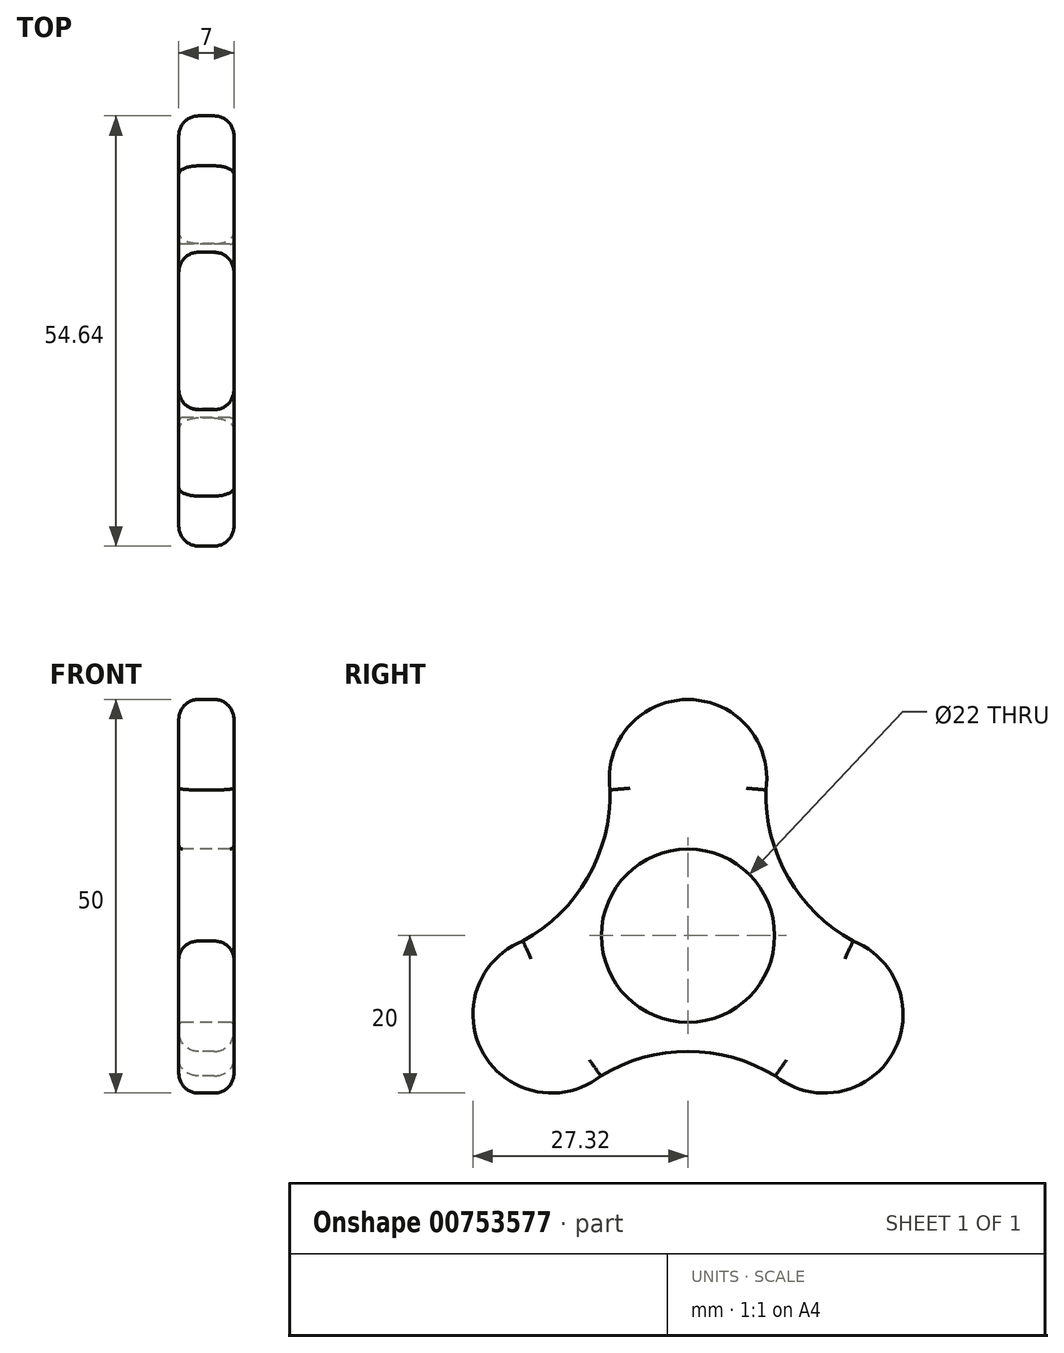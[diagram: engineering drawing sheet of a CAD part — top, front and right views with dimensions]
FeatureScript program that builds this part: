
annotation { "Feature Type Name" : "Feature", "Feature Type Description" : "" }
export const myFeature = defineFeature(function(context is Context, id is Id, definition is map)
    precondition{}
    {
        {
            var Q0;
            Q0=qCreatedBy(makeId("Right.planeOp"),FACE);
            var sketch = newSketch(context, id + "F0", { "sketchPlane" : qUnion([Q0])});
            skLineSegment(sketch, "E0", {"start": v(0, 0) * mm, "end": v(0, 20) * mm, "construction": true});
            skCircle(sketch, "E1", {"center": v(0, 20) * mm, "radius": 10 * mm});
            skCircle(sketch, "E2.1.0", {"center": v(-17.32, -10) * mm, "radius": 10 * mm});
            skCircle(sketch, "E2.2.0", {"center": v(17.32, -10) * mm, "radius": 10 * mm});
            skPoint(sketch, "E2.center", {"position": v(0, 0) * mm});
            skLineSegment(sketch, "E3", {"start": v(0, 20) * mm, "end": v(-17.32, -10) * mm, "construction": true});
            skLineSegment(sketch, "E4", {"start": v(0, 20) * mm, "end": v(-8.66, 25) * mm, "construction": true});
            skLineSegment(sketch, "E5", {"start": v(-17.32, -10) * mm, "end": v(-25.98, -5) * mm, "construction": true});
            skLineSegment(sketch, "E6", {"start": v(-21.65, -7.5) * mm, "end": v(-4.33, 22.5) * mm, "construction": true});
            skCircle(sketch, "E7", {"center": v(0, 0) * mm, "radius": 11 * mm});
            skLineSegment(sketch, "E8", {"start": v(-24.09, -6.1) * mm, "end": v(-6.77, 23.9) * mm, "construction": true});
            skArc(sketch, "E9", {"start": v(-20.97, -0.7) * mm, "mid": v(-12.74, 7.36) * mm, "end": v(-9.89, 18.5) * mm});
            skArc(sketch, "E10.1.0", {"start": v(11.08, -17.82) * mm, "mid": v(0, -14.72) * mm, "end": v(-11.08, -17.82) * mm});
            skArc(sketch, "E10.2.0", {"start": v(9.89, 18.5) * mm, "mid": v(12.74, 7.36) * mm, "end": v(20.97, -0.7) * mm});
            skSolve(sketch);
        }
        {
            var Q0;
            Q0 = qSketchRegion(id + "F0", true);
            extrude(context, id + "F1", {"entities" : qUnion([Q0]), "depth" : 7 * mm, "offsetDistance" : 25.4 * mm});
        }
        {
            var Q0;
            Q0=makeQuery(id+"F1.opExtrude","CAP_EDGE",EDGE,{"disambiguationData":[OSD([sQuery(id+"F0.wireOp",EDGE,"E9")])],"isStart":true});
            var Q1;
            Q1=makeQuery(id+"F1.opExtrude","CAP_EDGE",EDGE,{"disambiguationData":[OSD([sQuery(id+"F0.wireOp",EDGE,"E10.1.0")])],"isStart":true});
            var Q2;
            Q2=makeQuery(id+"F1.opExtrude","CAP_EDGE",EDGE,{"disambiguationData":[OSD([sQuery(id+"F0.wireOp",EDGE,"E10.2.0")])],"isStart":true});
            var Q3;
            Q3=makeQuery(id+"F1.opExtrude","CAP_EDGE",EDGE,{"disambiguationData":[OSD([sQuery(id+"F0.wireOp",EDGE,"E10.2.0")])],"isStart":false});
            var Q4;
            Q4=makeQuery(id+"F1.opExtrude","CAP_EDGE",EDGE,{"disambiguationData":[OSD([sQuery(id+"F0.wireOp",EDGE,"E9")])],"isStart":false});
            var Q5;
            Q5=makeQuery(id+"F1.opExtrude","CAP_EDGE",EDGE,{"disambiguationData":[OSD([sQuery(id+"F0.wireOp",EDGE,"E10.1.0")])],"isStart":false});
            var Q6;
            Q6=makeQuery(id+"F1.opExtrude","CAP_EDGE",EDGE,{"disambiguationData":[OSD([sQuery(id+"F0.wireOp",EDGE,"E2.1.0")])],"isStart":false});
            var Q7;
            Q7=makeQuery(id+"F1.opExtrude","CAP_EDGE",EDGE,{"disambiguationData":[OSD([sQuery(id+"F0.wireOp",EDGE,"E2.2.0")])],"isStart":false});
            var Q8;
            Q8=makeQuery(id+"F1.opExtrude","CAP_EDGE",EDGE,{"disambiguationData":[OSD([sQuery(id+"F0.wireOp",EDGE,"E1")])],"isStart":false});
            var Q9;
            Q9=makeQuery(id+"F1.opExtrude","CAP_EDGE",EDGE,{"disambiguationData":[OSD([sQuery(id+"F0.wireOp",EDGE,"E2.2.0")])],"isStart":true});
            var Q10;
            Q10=makeQuery(id+"F1.opExtrude","CAP_EDGE",EDGE,{"disambiguationData":[OSD([sQuery(id+"F0.wireOp",EDGE,"E2.1.0")])],"isStart":true});
            var Q11;
            Q11=makeQuery(id+"F1.opExtrude","CAP_EDGE",EDGE,{"disambiguationData":[OSD([sQuery(id+"F0.wireOp",EDGE,"E1")])],"isStart":true});
            fillet(context, id + "F2", {"entities" : qUnion([Q0, Q1, Q2, Q3, Q4, Q5, Q6, Q7, Q8, Q9, Q10, Q11]), "radius" : 2.5 * mm, "tangentPropagation" : true, "allowEdgeOverflow" : false});
        }
        {
            var Q0;
            Q0=makeQuery(id+"F1.opExtrude","CAP_EDGE",EDGE,{"disambiguationData":[OSD([sQuery(id+"F0.wireOp",EDGE,"E7")])],"isStart":true});
            var Q1;
            Q1=makeQuery(id+"F1.opExtrude","CAP_EDGE",EDGE,{"disambiguationData":[OSD([sQuery(id+"F0.wireOp",EDGE,"E7")])],"isStart":false});
            fillet(context, id + "F3", {"entities" : qUnion([Q0, Q1]), "radius" : .5 * mm, "tangentPropagation" : true, "allowEdgeOverflow" : false});
        }
    });
